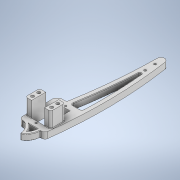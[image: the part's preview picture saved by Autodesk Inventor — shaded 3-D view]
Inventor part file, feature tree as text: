
AUTODESK INVENTOR PART (.ipt)
format: ipt  version: 2020.3 (Build 243373000, 373)  size: 383,488 bytes
history: native  units: mm
features: other x3, plane x3, sketch x2
ambient origin geometry x8: Origin, YZ Plane, XZ Plane, XY Plane, X Axis, Y Axis, Z Axis, Center Point
bodies: Solid1 (feature_tree)
feature tree (8):
  other  "LegEnd_Right_v2.ipt"
  plane  "Work Plane1"
  plane  "Work Plane2"
  plane  "Work Plane3"
  other  "Solid1::LegEnd_Right_v2.ipt"
  other  "TaggingFeature1"
  sketch  "Sketch1"  dims[d0=10.0mm]
  sketch  "Sketch3"  dims[d1=90.0deg d2=90.0deg d3=-7.5mm]
